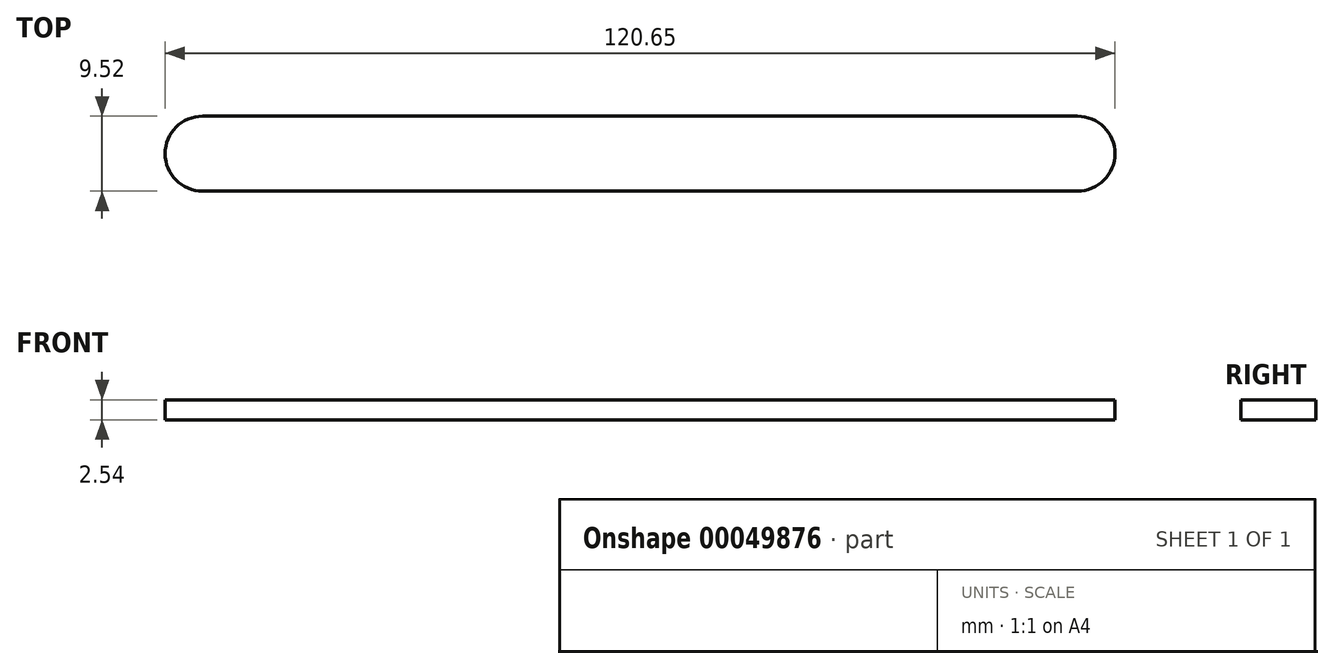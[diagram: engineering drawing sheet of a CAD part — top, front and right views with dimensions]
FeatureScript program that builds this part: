
annotation { "Feature Type Name" : "Feature", "Feature Type Description" : "" }
export const myFeature = defineFeature(function(context is Context, id is Id, definition is map)
    precondition{}
    {
        {
            var Q0;
            Q0=qCreatedBy(makeId("Top.planeOp"),FACE);
            var sketch = newSketch(context, id + "F0", { "sketchPlane" : qUnion([Q0])});
            skCircle(sketch, "E0", {"center": v(-55, 15.66) * mm, "radius": 4.76 * mm});
            skLineSegment(sketch, "E1", {"start": v(-55, 15.66) * mm, "end": v(-55, 20.42) * mm});
            skLineSegment(sketch, "E2", {"start": v(-55, 20.42) * mm, "end": v(-55, 10.9) * mm});
            skLineSegment(sketch, "E3", {"start": v(-55, 10.9) * mm, "end": v(-55, 20.42) * mm});
            skLineSegment(sketch, "E4", {"start": v(-55, 20.42) * mm, "end": v(56.12, 20.42) * mm});
            skLineSegment(sketch, "E5", {"start": v(56.12, 20.42) * mm, "end": v(56.12, 10.9) * mm});
            skLineSegment(sketch, "E6", {"start": v(56.12, 10.9) * mm, "end": v(56.12, 15.66) * mm});
            skCircle(sketch, "E7", {"center": v(56.12, 15.66) * mm, "radius": 4.76 * mm});
            skLineSegment(sketch, "E8", {"start": v(-55, 10.9) * mm, "end": v(56.12, 10.9) * mm});
            skSolve(sketch);
        }
        {
            var Q0;
            Q0 = qSketchRegion(id + "F0", true);
            extrude(context, id + "F1", {"entities" : qUnion([Q0]), "depth" : 2.54 * mm});
        }
    });
